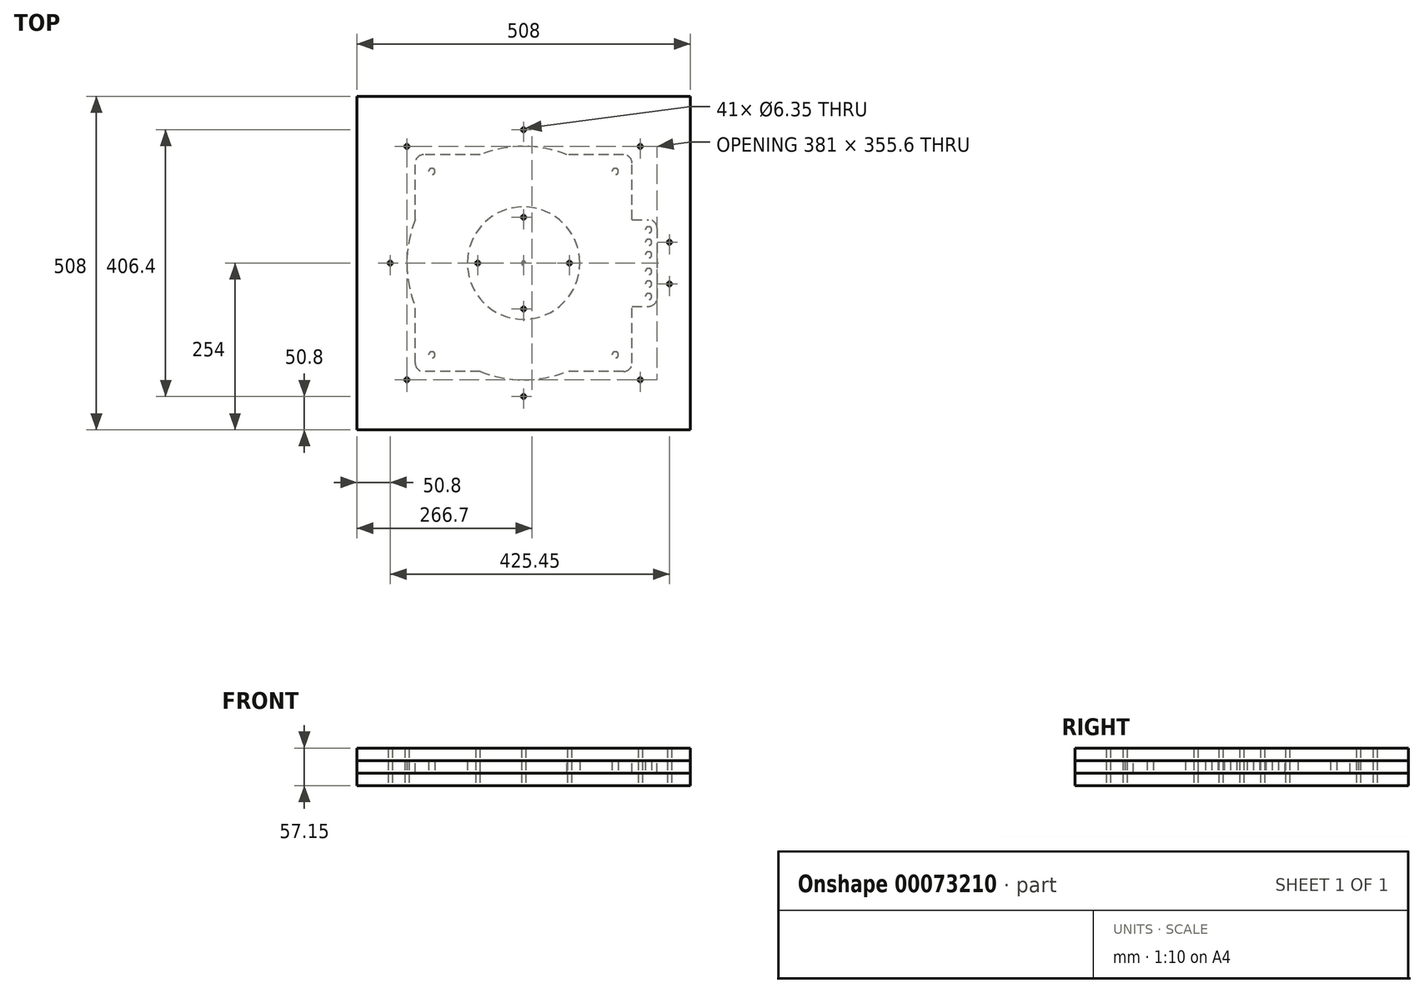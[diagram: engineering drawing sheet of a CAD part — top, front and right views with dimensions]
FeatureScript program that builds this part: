
annotation { "Feature Type Name" : "Feature", "Feature Type Description" : "" }
export const myFeature = defineFeature(function(context is Context, id is Id, definition is map)
    precondition{}
    {
        {
            var Q0;
            Q0=qCreatedBy(makeId("Top.planeOp"),FACE);
            var sketch = newSketch(context, id + "F0", { "sketchPlane" : qUnion([Q0])});
            skLineSegment(sketch, "E0.rect.bottom", {"start": v(254, -254) * mm, "end": v(-254, -254) * mm});
            skLineSegment(sketch, "E0.rect.top", {"start": v(254, 254) * mm, "end": v(-254, 254) * mm});
            skLineSegment(sketch, "E0.rect.left", {"start": v(254, -254) * mm, "end": v(254, 254) * mm});
            skLineSegment(sketch, "E0.rect.right", {"start": v(-254, -254) * mm, "end": v(-254, 254) * mm});
            skPoint(sketch, "E0.rect.middle", {"position": v(0, 0) * mm});
            skSolve(sketch);
        }
        {
            var Q0;
            Q0=makeQuery(id+"F0.imprint","IMPRINT",FACE,{"disambiguationData":[TD([[makeQuery(id+"F0.imprint","IMPRINT",EDGE,{"derivedFrom":sQuery(id+"F0.wireOp",EDGE,"E0.rect.bottom")}),-1.0]])]});
            extrude(context, id + "F1", {"entities" : qUnion([Q0]), "depth" : 19.05 * mm});
        }
        {
            var Q0;
            Q0=makeQuery(id+"F1.opExtrude","CAP_FACE",FACE,{"disambiguationData":[OSD([sQuery(id+"F0.wireOp",EDGE,"E0.rect.bottom"),sQuery(id+"F0.wireOp",EDGE,"E0.rect.top"),sQuery(id+"F0.wireOp",EDGE,"E0.rect.left"),sQuery(id+"F0.wireOp",EDGE,"E0.rect.right")])],"isStart":false});
            var sketch = newSketch(context, id + "F2", { "sketchPlane" : qUnion([Q0])});
            skLineSegment(sketch, "E1.bottom", {"start": v(-254, 254) * mm, "end": v(254, 254) * mm});
            skLineSegment(sketch, "E1.top", {"start": v(-254, -254) * mm, "end": v(254, -254) * mm});
            skLineSegment(sketch, "E1.left", {"start": v(-254, 254) * mm, "end": v(-254, -254) * mm});
            skLineSegment(sketch, "E1.right", {"start": v(254, 254) * mm, "end": v(254, -254) * mm});
            skCircle(sketch, "E2", {"center": v(0, 0) * mm, "radius": 177.8 * mm});
            skCircle(sketch, "E3", {"center": v(0, 0) * mm, "radius": 85.73 * mm});
            skSolve(sketch);
        }
        {
            var Q0;
            Q0=makeQuery(id+"F2.imprint","IMPRINT",FACE,{"disambiguationData":[TD([[makeQuery(id+"F2.imprint","IMPRINT",EDGE,{"derivedFrom":sQuery(id+"F2.wireOp",EDGE,"E1.bottom")}),1.0]])]});
            var Q1;
            Q1=makeQuery(id+"F2.imprint","IMPRINT",FACE,{"disambiguationData":[TD([[makeQuery(id+"F2.imprint","IMPRINT",EDGE,{"derivedFrom":sQuery(id+"F2.wireOp",EDGE,"E3")}),1.0]])]});
            extrude(context, id + "F3", {"entities" : qUnion([Q0, Q1]), "depth" : 19.05 * mm});
        }
        {
            var Q0;
            Q0=makeQuery(id+"F3.opExtrude","CAP_FACE",FACE,{"disambiguationData":[OSD([sQuery(id+"F2.wireOp",EDGE,"E1.bottom"),sQuery(id+"F2.wireOp",EDGE,"E1.top"),sQuery(id+"F2.wireOp",EDGE,"E1.left"),sQuery(id+"F2.wireOp",EDGE,"E1.right"),sQuery(id+"F2.wireOp",EDGE,"E2")])],"isStart":false});
            var sketch = newSketch(context, id + "F4", { "sketchPlane" : qUnion([Q0])});
            skLineSegment(sketch, "E4.rect.bottom", {"start": v(152.4, -165.1) * mm, "end": v(-152.4, -165.1) * mm});
            skLineSegment(sketch, "E4.rect.top", {"start": v(152.4, 165.1) * mm, "end": v(-152.4, 165.1) * mm});
            skLineSegment(sketch, "E4.rect.left", {"start": v(165.1, -152.4) * mm, "end": v(165.1, 152.4) * mm});
            skLineSegment(sketch, "E4.rect.right", {"start": v(-165.1, -152.4) * mm, "end": v(-165.1, 152.4) * mm});
            skPoint(sketch, "E4.rect.middle", {"position": v(0, 0) * mm});
            skPoint(sketch, "E5.visualSharp", {"position": v(-165.1, 165.1) * mm});
            skArc(sketch, "E5.filletArc", {"start": v(-152.4, 165.1) * mm, "mid": v(-161.38, 161.38) * mm, "end": v(-165.1, 152.4) * mm});
            skPoint(sketch, "E6.visualSharp", {"position": v(165.1, 165.1) * mm});
            skArc(sketch, "E6.filletArc", {"start": v(165.1, 152.4) * mm, "mid": v(161.38, 161.38) * mm, "end": v(152.4, 165.1) * mm});
            skPoint(sketch, "E7.visualSharp", {"position": v(165.1, -165.1) * mm});
            skArc(sketch, "E7.filletArc", {"start": v(152.4, -165.1) * mm, "mid": v(161.38, -161.38) * mm, "end": v(165.1, -152.4) * mm});
            skPoint(sketch, "E8.visualSharp", {"position": v(-165.1, -165.1) * mm});
            skArc(sketch, "E8.filletArc", {"start": v(-165.1, -152.4) * mm, "mid": v(-161.38, -161.38) * mm, "end": v(-152.4, -165.1) * mm});
            skLineSegment(sketch, "E9.bottom", {"start": v(165.1, 66) * mm, "end": v(190.5, 66) * mm});
            skLineSegment(sketch, "E9.top", {"start": v(165.1, -66) * mm, "end": v(190.5, -66) * mm});
            skLineSegment(sketch, "E9.left", {"start": v(165.1, 66) * mm, "end": v(165.1, -66) * mm});
            skLineSegment(sketch, "E9.right", {"start": v(203.2, 53.3) * mm, "end": v(203.2, -53.3) * mm});
            skPoint(sketch, "E10.visualSharp", {"position": v(203.2, 66) * mm});
            skArc(sketch, "E10.filletArc", {"start": v(203.2, 53.3) * mm, "mid": v(199.48, 62.27) * mm, "end": v(190.5, 66) * mm});
            skPoint(sketch, "E11.visualSharp", {"position": v(203.2, -66) * mm});
            skArc(sketch, "E11.filletArc", {"start": v(190.5, -66) * mm, "mid": v(199.48, -62.27) * mm, "end": v(203.2, -53.3) * mm});
            skSolve(sketch);
        }
        {
            var Q0;
            {var subQ0=sQuery(id+"F4.wireOp",EDGE,"E5.filletArc");Q0=makeQuery(id+"F4.imprint","IMPRINT",FACE,{"disambiguationData":[TD([[makeQuery(id+"F4.imprint","IMPRINT",EDGE,{"derivedFrom":subQ0}),1.0]])]});}
            var Q1;
            {var subQ0=sQuery(id+"F4.wireOp",EDGE,"E6.filletArc");Q1=makeQuery(id+"F4.imprint","IMPRINT",FACE,{"disambiguationData":[TD([[makeQuery(id+"F4.imprint","IMPRINT",EDGE,{"derivedFrom":subQ0}),1.0]])]});}
            var Q2;
            {var subQ0=sQuery(id+"F4.wireOp",EDGE,"E7.filletArc");Q2=makeQuery(id+"F4.imprint","IMPRINT",FACE,{"disambiguationData":[TD([[makeQuery(id+"F4.imprint","IMPRINT",EDGE,{"derivedFrom":subQ0}),1.0]])]});}
            var Q3;
            {var subQ0=sQuery(id+"F4.wireOp",EDGE,"E8.filletArc");Q3=makeQuery(id+"F4.imprint","IMPRINT",FACE,{"disambiguationData":[TD([[makeQuery(id+"F4.imprint","IMPRINT",EDGE,{"derivedFrom":subQ0}),1.0]])]});}
            var Q4;
            {var subQ1=sQuery(id+"F4.wireOp",EDGE,"E9.bottom");Q4=makeQuery(id+"F4.imprint","IMPRINT",FACE,{"disambiguationData":[TD([[makeQuery(id+"F4.imprint","IMPRINT",EDGE,{"derivedFrom":subQ1}),-1.0]])]});}
            extrude(context, id + "F5", {"entities" : qUnion([Q0, Q1, Q2, Q3, Q4]), "operationType" : NewBodyOperationType.REMOVE, "oppositeDirection" : true, "depth" : 19.05 * mm});
        }
        {
            var Q0;
            Q0=makeQuery(id+"F3.opExtrude","CAP_FACE",FACE,{"disambiguationData":[OSD([sQuery(id+"F2.wireOp",EDGE,"E1.bottom"),sQuery(id+"F2.wireOp",EDGE,"E1.top"),sQuery(id+"F2.wireOp",EDGE,"E1.left"),sQuery(id+"F2.wireOp",EDGE,"E1.right"),sQuery(id+"F2.wireOp",EDGE,"E2")])],"isStart":false});
            var sketch = newSketch(context, id + "F6", { "sketchPlane" : qUnion([Q0])});
            skCircle(sketch, "E12", {"center": v(-177.8, 177.8) * mm, "radius": 3.18 * mm});
            skCircle(sketch, "E13", {"center": v(0, -203.2) * mm, "radius": 3.18 * mm});
            skCircle(sketch, "E14", {"center": v(-203.2, 0) * mm, "radius": 3.18 * mm});
            skCircle(sketch, "E15", {"center": v(0, 203.2) * mm, "radius": 3.18 * mm});
            skCircle(sketch, "E16", {"center": v(222.25, 31.75) * mm, "radius": 3.18 * mm});
            skCircle(sketch, "E17", {"center": v(222.25, -31.75) * mm, "radius": 3.18 * mm});
            skCircle(sketch, "E18", {"center": v(0, 69.85) * mm, "radius": 3.18 * mm});
            skCircle(sketch, "E19", {"center": v(0, 0) * mm, "radius": 3.18 * mm});
            skCircle(sketch, "E20.1.0", {"center": v(-177.8, -177.8) * mm, "radius": 3.18 * mm});
            skCircle(sketch, "E20.2.0", {"center": v(177.8, -177.8) * mm, "radius": 3.18 * mm});
            skCircle(sketch, "E20.3.0", {"center": v(177.8, 177.8) * mm, "radius": 3.18 * mm});
            skCircle(sketch, "E21.1.0", {"center": v(-69.85, 0) * mm, "radius": 3.18 * mm});
            skCircle(sketch, "E21.2.0", {"center": v(0, -69.85) * mm, "radius": 3.18 * mm});
            skCircle(sketch, "E21.3.0", {"center": v(69.85, 0) * mm, "radius": 3.18 * mm});
            skSolve(sketch);
        }
        {
            var Q0;
            Q0=makeQuery(id+"F6.imprint","IMPRINT",FACE,{"disambiguationData":[TD([[makeQuery(id+"F6.imprint","IMPRINT",EDGE,{"derivedFrom":sQuery(id+"F6.wireOp",EDGE,"E12")}),-1.0]])]});
            var sketch = newSketch(context, id + "F7", { "sketchPlane" : qUnion([Q0])});
            skLineSegment(sketch, "E22.rect.bottom", {"start": v(254, -254) * mm, "end": v(-254, -254) * mm});
            skLineSegment(sketch, "E22.rect.top", {"start": v(254, 254) * mm, "end": v(-254, 254) * mm});
            skLineSegment(sketch, "E22.rect.left", {"start": v(254, -254) * mm, "end": v(254, 254) * mm});
            skLineSegment(sketch, "E22.rect.right", {"start": v(-254, -254) * mm, "end": v(-254, 254) * mm});
            skPoint(sketch, "E22.rect.middle", {"position": v(0, 0) * mm});
            skSolve(sketch);
        }
        {
            var Q0;
            Q0 = qSketchRegion(id + "F7", true);
            extrude(context, id + "F8", {"entities" : qUnion([Q0]), "depth" : 19.05 * mm});
        }
        {
            var Q0;
            Q0=makeQuery(id+"F6.imprint","IMPRINT",FACE,{"disambiguationData":[TD([[makeQuery(id+"F6.imprint","IMPRINT",EDGE,{"derivedFrom":sQuery(id+"F6.wireOp",EDGE,"E20.2.0")}),1.0]])]});
            var Q1;
            Q1=makeQuery(id+"F6.imprint","IMPRINT",FACE,{"disambiguationData":[TD([[makeQuery(id+"F6.imprint","IMPRINT",EDGE,{"derivedFrom":sQuery(id+"F6.wireOp",EDGE,"E17")}),1.0]])]});
            var Q2;
            Q2=makeQuery(id+"F6.imprint","IMPRINT",FACE,{"disambiguationData":[TD([[makeQuery(id+"F6.imprint","IMPRINT",EDGE,{"derivedFrom":sQuery(id+"F6.wireOp",EDGE,"E16")}),1.0]])]});
            var Q3;
            Q3=makeQuery(id+"F6.imprint","IMPRINT",FACE,{"disambiguationData":[TD([[makeQuery(id+"F6.imprint","IMPRINT",EDGE,{"derivedFrom":sQuery(id+"F6.wireOp",EDGE,"E20.3.0")}),1.0]])]});
            var Q4;
            Q4=makeQuery(id+"F6.imprint","IMPRINT",FACE,{"disambiguationData":[TD([[makeQuery(id+"F6.imprint","IMPRINT",EDGE,{"derivedFrom":sQuery(id+"F6.wireOp",EDGE,"E15")}),1.0]])]});
            var Q5;
            Q5=makeQuery(id+"F6.imprint","IMPRINT",FACE,{"disambiguationData":[TD([[makeQuery(id+"F6.imprint","IMPRINT",EDGE,{"derivedFrom":sQuery(id+"F6.wireOp",EDGE,"E12")}),1.0]])]});
            var Q6;
            Q6=makeQuery(id+"F6.imprint","IMPRINT",FACE,{"disambiguationData":[TD([[makeQuery(id+"F6.imprint","IMPRINT",EDGE,{"derivedFrom":sQuery(id+"F6.wireOp",EDGE,"E14")}),1.0]])]});
            var Q7;
            Q7=makeQuery(id+"F6.imprint","IMPRINT",FACE,{"disambiguationData":[TD([[makeQuery(id+"F6.imprint","IMPRINT",EDGE,{"derivedFrom":sQuery(id+"F6.wireOp",EDGE,"E20.1.0")}),1.0]])]});
            var Q8;
            Q8=makeQuery(id+"F6.imprint","IMPRINT",FACE,{"disambiguationData":[TD([[makeQuery(id+"F6.imprint","IMPRINT",EDGE,{"derivedFrom":sQuery(id+"F6.wireOp",EDGE,"E13")}),1.0]])]});
            var Q9;
            Q9=makeQuery(id+"F6.imprint","IMPRINT",FACE,{"disambiguationData":[TD([[makeQuery(id+"F6.imprint","IMPRINT",EDGE,{"derivedFrom":sQuery(id+"F6.wireOp",EDGE,"E21.2.0")}),1.0]])]});
            var Q10;
            Q10=makeQuery(id+"F6.imprint","IMPRINT",FACE,{"disambiguationData":[TD([[makeQuery(id+"F6.imprint","IMPRINT",EDGE,{"derivedFrom":sQuery(id+"F6.wireOp",EDGE,"E21.1.0")}),1.0]])]});
            var Q11;
            Q11=makeQuery(id+"F6.imprint","IMPRINT",FACE,{"disambiguationData":[TD([[makeQuery(id+"F6.imprint","IMPRINT",EDGE,{"derivedFrom":sQuery(id+"F6.wireOp",EDGE,"E18")}),1.0]])]});
            var Q12;
            Q12=makeQuery(id+"F6.imprint","IMPRINT",FACE,{"disambiguationData":[TD([[makeQuery(id+"F6.imprint","IMPRINT",EDGE,{"derivedFrom":sQuery(id+"F6.wireOp",EDGE,"E21.3.0")}),1.0]])]});
            extrude(context, id + "F9", {"entities" : qUnion([Q0, Q1, Q2, Q3, Q4, Q5, Q6, Q7, Q8, Q9, Q10, Q11, Q12]), "operationType" : NewBodyOperationType.REMOVE, "depth" : 25.4 * mm, "hasSecondDirection" : true, "secondDirectionOppositeDirection" : true, "secondDirectionDepth" : 44.45 * mm});
        }
        {
            var Q0;
            Q0=makeQuery(id+"F6.imprint","IMPRINT",FACE,{"disambiguationData":[TD([[makeQuery(id+"F6.imprint","IMPRINT",EDGE,{"derivedFrom":sQuery(id+"F6.wireOp",EDGE,"E19")}),1.0]])]});
            extrude(context, id + "F10", {"entities" : qUnion([Q0]), "operationType" : NewBodyOperationType.REMOVE, "oppositeDirection" : true, "depth" : 50.8 * mm});
        }
        {
            var Q0;
            Q0=makeQuery(id+"F1.opExtrude","CAP_FACE",FACE,{"disambiguationData":[OSD([sQuery(id+"F0.wireOp",EDGE,"E0.rect.bottom"),sQuery(id+"F0.wireOp",EDGE,"E0.rect.top"),sQuery(id+"F0.wireOp",EDGE,"E0.rect.left"),sQuery(id+"F0.wireOp",EDGE,"E0.rect.right")])],"isStart":false});
            var sketch = newSketch(context, id + "F11", { "sketchPlane" : qUnion([Q0])});
            skCircle(sketch, "E23", {"center": v(-139.7, 139.7) * mm, "radius": 4.76 * mm});
            skCircle(sketch, "E24.1.0", {"center": v(-139.7, -139.7) * mm, "radius": 4.76 * mm});
            skCircle(sketch, "E24.2.0", {"center": v(139.7, -139.7) * mm, "radius": 4.76 * mm});
            skCircle(sketch, "E24.3.0", {"center": v(139.7, 139.7) * mm, "radius": 4.76 * mm});
            skPoint(sketch, "E24.center", {"position": v(0, 0) * mm});
            skCircle(sketch, "E25", {"center": v(190.5, 50.8) * mm, "radius": 4.76 * mm});
            skCircle(sketch, "E26", {"center": v(190.5, 31.75) * mm, "radius": 4.76 * mm});
            skCircle(sketch, "E27", {"center": v(190.5, 12.7) * mm, "radius": 4.76 * mm});
            skCircle(sketch, "E28", {"center": v(190.5, -12.7) * mm, "radius": 4.76 * mm});
            skCircle(sketch, "E29", {"center": v(190.5, -31.75) * mm, "radius": 4.76 * mm});
            skCircle(sketch, "E30", {"center": v(190.5, -50.8) * mm, "radius": 4.76 * mm});
            skSolve(sketch);
        }
        {
            var Q0;
            Q0 = qSketchRegion(id + "F11", true);
            extrude(context, id + "F12", {"entities" : qUnion([Q0]), "operationType" : NewBodyOperationType.ADD, "depth" : 19.05 * mm});
        }
    });
